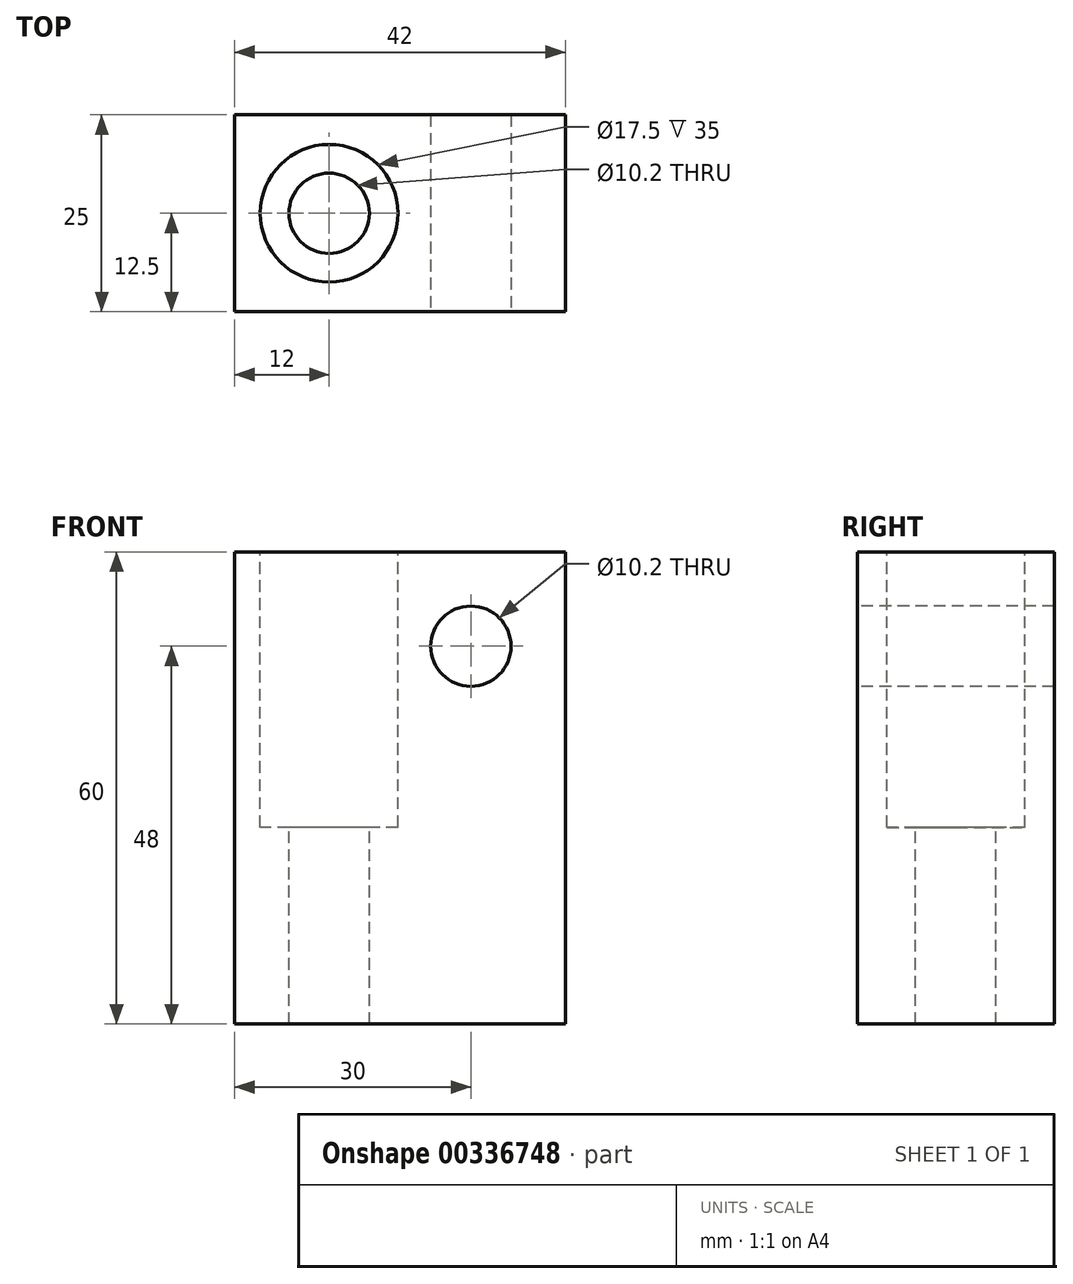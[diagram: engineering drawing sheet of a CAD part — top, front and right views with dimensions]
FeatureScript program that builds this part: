
annotation { "Feature Type Name" : "Feature", "Feature Type Description" : "" }
export const myFeature = defineFeature(function(context is Context, id is Id, definition is map)
    precondition{}
    {
        {
            var Q0;
            Q0=qCreatedBy(makeId("Top.planeOp"),FACE);
            var sketch = newSketch(context, id + "F0", { "sketchPlane" : qUnion([Q0])});
            skLineSegment(sketch, "E0", {"start": v(0, 0) * mm, "end": v(42, 0) * mm});
            skLineSegment(sketch, "E1", {"start": v(42, 0) * mm, "end": v(42, 25) * mm});
            skLineSegment(sketch, "E2", {"start": v(42, 25) * mm, "end": v(0, 25) * mm});
            skLineSegment(sketch, "E3", {"start": v(0, 25) * mm, "end": v(0, 0) * mm});
            skSolve(sketch);
        }
        {
            var Q0;
            Q0=qSketchRegion(id+"F0",true);
            extrude(context, id + "F1", {"entities" : qUnion([Q0]), "depth" : 60 * mm});
        }
        {
            var Q0;
            Q0=makeQuery(id+"F1.opExtrude","CAP_FACE",FACE,{"disambiguationData":[OSD([sQuery(id+"F0.wireOp",EDGE,"E0"),sQuery(id+"F0.wireOp",EDGE,"E1"),sQuery(id+"F0.wireOp",EDGE,"E2"),sQuery(id+"F0.wireOp",EDGE,"E3")])],"isStart":false});
            cPlane(context, id + "F2", {"entities" : qUnion([Q0]), "cplaneType" : CPlaneType.OFFSET, "offset" : 0 * mm, "width" : 150 * mm, "height" : 150 * mm});
        }
        {
            var Q0;
            Q0=qCreatedBy(id+"F2.planeOp",FACE);
            var sketch = newSketch(context, id + "F3", { "sketchPlane" : qUnion([Q0])});
            skCircle(sketch, "E4", {"center": v(12, 12.5) * mm, "radius": 8.75 * mm});
            skSolve(sketch);
        }
        {
            var Q0;
            Q0=qSketchRegion(id+"F3",true);
            extrude(context, id + "F4", {"entities" : qUnion([Q0]), "operationType" : NewBodyOperationType.REMOVE, "oppositeDirection" : true, "depth" : 35 * mm});
        }
        {
            var Q0;
            Q0=makeQuery(id+"F1.opExtrude","CAP_FACE",FACE,{"disambiguationData":[OSD([sQuery(id+"F0.wireOp",EDGE,"E0"),sQuery(id+"F0.wireOp",EDGE,"E1"),sQuery(id+"F0.wireOp",EDGE,"E2"),sQuery(id+"F0.wireOp",EDGE,"E3")])],"isStart":false});
            cPlane(context, id + "F5", {"entities" : qUnion([Q0]), "cplaneType" : CPlaneType.OFFSET, "offset" : 0 * mm, "width" : 150 * mm, "height" : 150 * mm});
        }
        {
            var Q0;
            Q0=qCreatedBy(id+"F5.planeOp",FACE);
            var sketch = newSketch(context, id + "F6", { "sketchPlane" : qUnion([Q0])});
            skCircle(sketch, "E5", {"center": v(12, 12.5) * mm, "radius": 5.1 * mm});
            skSolve(sketch);
        }
        {
            var Q0;
            Q0=qSketchRegion(id+"F6",true);
            extrude(context, id + "F7", {"entities" : qUnion([Q0]), "operationType" : NewBodyOperationType.REMOVE, "oppositeDirection" : true, "depth" : 100 * mm});
        }
        {
            var Q0;
            Q0=makeQuery(id+"F1.opExtrude","SWEPT_FACE",FACE,{"disambiguationData":[OSD([sQuery(id+"F0.wireOp",EDGE,"E0")])]});
            cPlane(context, id + "F8", {"entities" : qUnion([Q0]), "cplaneType" : CPlaneType.OFFSET, "offset" : 0 * mm, "width" : 150 * mm, "height" : 150 * mm});
        }
        {
            var Q0;
            Q0=qCreatedBy(id+"F8.planeOp",FACE);
            var sketch = newSketch(context, id + "F9", { "sketchPlane" : qUnion([Q0])});
            skCircle(sketch, "E6", {"center": v(30, 48) * mm, "radius": 5.1 * mm});
            skSolve(sketch);
        }
        {
            var Q0;
            Q0=qSketchRegion(id+"F9",true);
            extrude(context, id + "F10", {"entities" : qUnion([Q0]), "operationType" : NewBodyOperationType.REMOVE, "oppositeDirection" : true, "depth" : 80 * mm});
        }
    });
